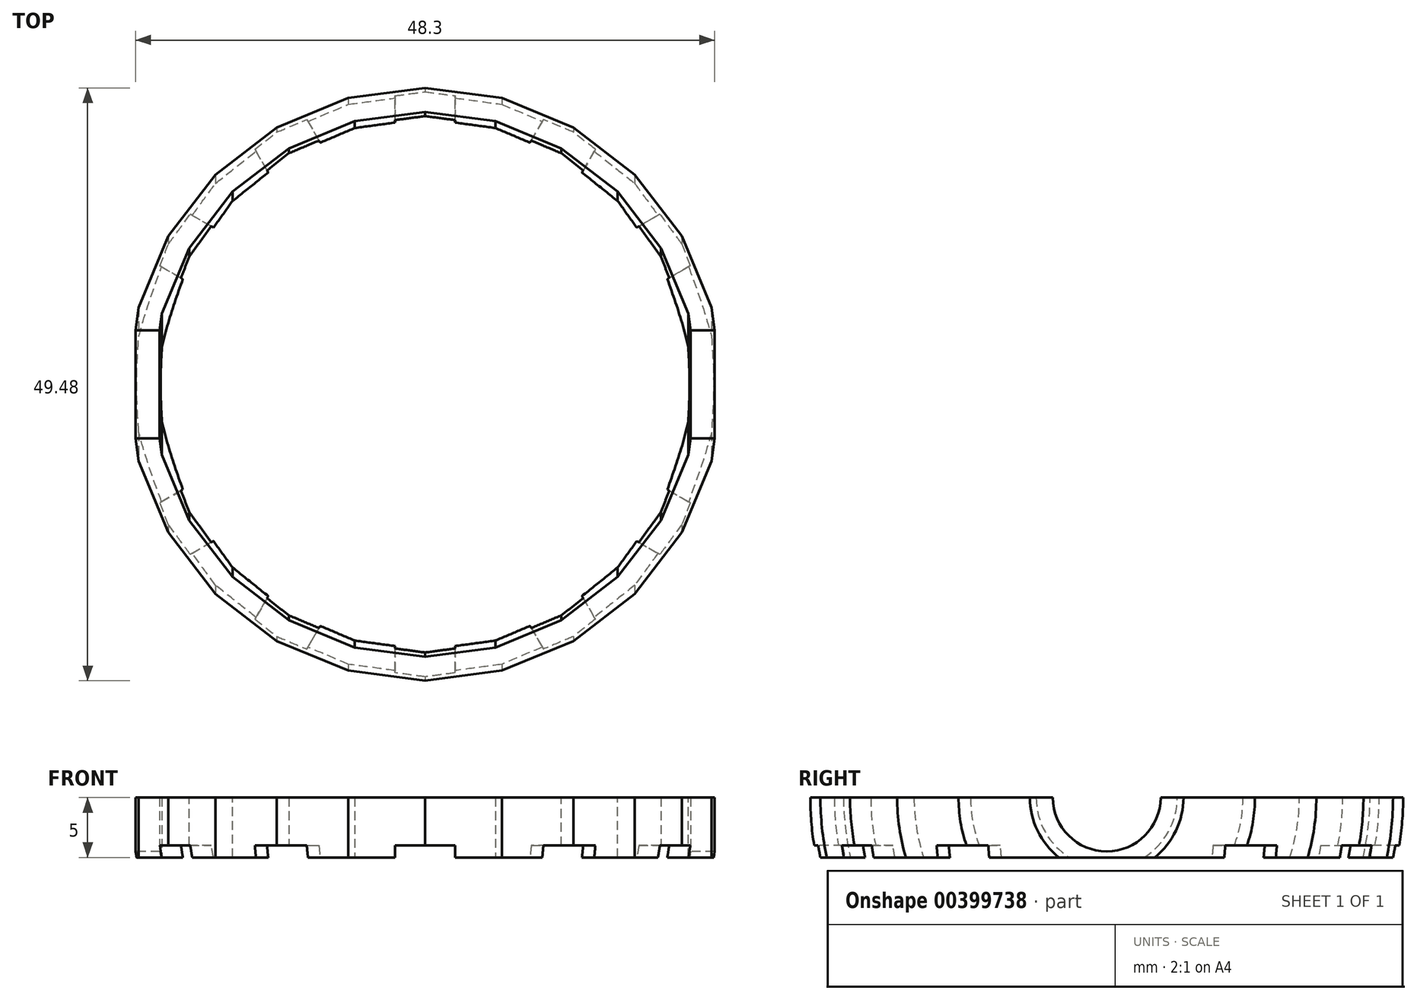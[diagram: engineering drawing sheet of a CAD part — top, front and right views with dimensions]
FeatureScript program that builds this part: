
annotation { "Feature Type Name" : "Feature", "Feature Type Description" : "" }
export const myFeature = defineFeature(function(context is Context, id is Id, definition is map)
    precondition{}
    {
        {
            var Q0;
            Q0=qCreatedBy(makeId("Top.planeOp"),FACE);
            var sketch = newSketch(context, id + "F0", { "sketchPlane" : qUnion([Q0])});
            skLineSegment(sketch, "E0", {"start": v(-24.74, 0) * mm, "end": v(24.74, 0) * mm});
            skLineSegment(sketch, "E1", {"start": v(-24.74, 0) * mm, "end": v(-22.74, 0) * mm});
            skLineSegment(sketch, "E2", {"start": v(24.74, 0) * mm, "end": v(22.74, 0) * mm});
            skLineSegment(sketch, "E3", {"start": v(0, 0) * mm, "end": v(-21.43, -12.37) * mm});
            skLineSegment(sketch, "E4", {"start": v(0, 0) * mm, "end": v(-23.9, -6.4) * mm});
            skLineSegment(sketch, "E5", {"start": v(-23.9, -6.4) * mm, "end": v(0, 0) * mm});
            skLineSegment(sketch, "E6", {"start": v(0, 0) * mm, "end": v(-17.5, -17.5) * mm});
            skLineSegment(sketch, "E7", {"start": v(-17.5, -17.5) * mm, "end": v(0, 0) * mm});
            skLineSegment(sketch, "E8", {"start": v(0, 0) * mm, "end": v(12.37, -21.43) * mm});
            skLineSegment(sketch, "E9", {"start": v(12.37, -21.43) * mm, "end": v(0, 0) * mm});
            skLineSegment(sketch, "E10", {"start": v(0, 0) * mm, "end": v(17.5, -17.5) * mm});
            skLineSegment(sketch, "E11", {"start": v(17.5, -17.5) * mm, "end": v(0, 0) * mm});
            skLineSegment(sketch, "E12", {"start": v(0, 0) * mm, "end": v(21.43, -12.37) * mm});
            skLineSegment(sketch, "E13", {"start": v(0, 0) * mm, "end": v(-12.37, -21.43) * mm});
            skLineSegment(sketch, "E14", {"start": v(-12.37, -21.43) * mm, "end": v(0, 0) * mm});
            skLineSegment(sketch, "E15", {"start": v(0, 0) * mm, "end": v(-6.4, -23.9) * mm});
            skLineSegment(sketch, "E16", {"start": v(0, 0) * mm, "end": v(6.4, -23.9) * mm});
            skLineSegment(sketch, "E17", {"start": v(0, 0) * mm, "end": v(23.9, -6.4) * mm});
            skLineSegment(sketch, "E18", {"start": v(0, 0) * mm, "end": v(0, -24.74) * mm});
            skSolve(sketch);
        }
        {
            var Q0;
            Q0=qCreatedBy(makeId("Top.planeOp"),FACE);
            var sketch = newSketch(context, id + "F1", { "sketchPlane" : qUnion([Q0])});
            skLineSegment(sketch, "E19", {"start": v(-24.74, 0) * mm, "end": v(-23.9, -6.4) * mm});
            skLineSegment(sketch, "E20", {"start": v(-23.9, -6.4) * mm, "end": v(-21.43, -12.37) * mm});
            skLineSegment(sketch, "E21", {"start": v(-21.43, -12.37) * mm, "end": v(-17.5, -17.5) * mm});
            skLineSegment(sketch, "E22", {"start": v(-17.5, -17.5) * mm, "end": v(-12.37, -21.43) * mm});
            skLineSegment(sketch, "E23", {"start": v(-12.37, -21.43) * mm, "end": v(-6.4, -23.9) * mm});
            skLineSegment(sketch, "E24", {"start": v(-6.4, -23.9) * mm, "end": v(0, -24.74) * mm});
            skLineSegment(sketch, "E25", {"start": v(0, -24.74) * mm, "end": v(6.4, -23.9) * mm});
            skLineSegment(sketch, "E26", {"start": v(6.4, -23.9) * mm, "end": v(12.37, -21.43) * mm});
            skLineSegment(sketch, "E27", {"start": v(12.37, -21.43) * mm, "end": v(17.5, -17.5) * mm});
            skLineSegment(sketch, "E28", {"start": v(17.5, -17.5) * mm, "end": v(21.43, -12.37) * mm});
            skLineSegment(sketch, "E29", {"start": v(21.43, -12.37) * mm, "end": v(23.9, -6.4) * mm});
            skLineSegment(sketch, "E30", {"start": v(23.9, -6.4) * mm, "end": v(24.74, 0) * mm});
            skLineSegment(sketch, "E31", {"start": v(-22.74, 0) * mm, "end": v(-21.97, -5.89) * mm});
            skLineSegment(sketch, "E32", {"start": v(-21.97, -5.89) * mm, "end": v(-19.7, -11.37) * mm});
            skLineSegment(sketch, "E33", {"start": v(-19.7, -11.37) * mm, "end": v(-16.08, -16.08) * mm});
            skLineSegment(sketch, "E34", {"start": v(-16.08, -16.08) * mm, "end": v(-11.37, -19.7) * mm});
            skLineSegment(sketch, "E35", {"start": v(-11.37, -19.7) * mm, "end": v(-5.89, -21.97) * mm});
            skLineSegment(sketch, "E36", {"start": v(-5.89, -21.97) * mm, "end": v(0, -22.74) * mm});
            skLineSegment(sketch, "E37", {"start": v(0, -22.74) * mm, "end": v(5.89, -21.97) * mm});
            skLineSegment(sketch, "E38", {"start": v(5.89, -21.97) * mm, "end": v(11.37, -19.7) * mm});
            skLineSegment(sketch, "E39", {"start": v(11.37, -19.7) * mm, "end": v(16.08, -16.08) * mm});
            skLineSegment(sketch, "E40", {"start": v(16.08, -16.08) * mm, "end": v(19.7, -11.37) * mm});
            skLineSegment(sketch, "E41", {"start": v(19.7, -11.37) * mm, "end": v(21.97, -5.89) * mm});
            skLineSegment(sketch, "E42", {"start": v(21.97, -5.89) * mm, "end": v(22.74, 0) * mm});
            skLineSegment(sketch, "E43", {"start": v(-24.74, 0) * mm, "end": v(-22.74, 0) * mm});
            skLineSegment(sketch, "E44", {"start": v(22.74, 0) * mm, "end": v(24.74, 0) * mm});
            skSolve(sketch);
        }
        {
            var Q0;
            Q0=qSketchRegion(id+"F1",true);
            var Q1;
            Q1=sQuery(id+"F0.wireOp",EDGE,"E0");
            revolve(context, id + "F2", {"entities" : qUnion([Q0]), "axis" : qUnion([Q1]), "revolveType" : RevolveType.FULL});
        }
        {
            var Q0;
            Q0=qCreatedBy(makeId("Top.planeOp"),FACE);
            var sketch = newSketch(context, id + "F3", { "sketchPlane" : qUnion([Q0])});
            skLineSegment(sketch, "E45.bottom", {"start": v(-24.99, 25) * mm, "end": v(24.99, 25) * mm});
            skLineSegment(sketch, "E45.top", {"start": v(-24.99, -25) * mm, "end": v(24.99, -25) * mm});
            skLineSegment(sketch, "E45.left", {"start": v(-24.99, 25) * mm, "end": v(-24.99, -25) * mm});
            skLineSegment(sketch, "E45.right", {"start": v(24.99, 25) * mm, "end": v(24.99, -25) * mm});
            skPoint(sketch, "E45.middle", {"position": v(0, 0) * mm});
            skSolve(sketch);
        }
        {
            var Q0;
            Q0=qSketchRegion(id+"F3",true);
            extrude(context, id + "F4", {"entities" : qUnion([Q0]), "operationType" : NewBodyOperationType.REMOVE, "depth" : 25 * mm});
        }
        {
            var Q0;
            Q0=qCreatedBy(makeId("Top.planeOp"),FACE);
            var sketch = newSketch(context, id + "F5", { "sketchPlane" : qUnion([Q0])});
            skLineSegment(sketch, "E46", {"start": v(-22.74, 0) * mm, "end": v(-21.97, -5.89) * mm});
            skLineSegment(sketch, "E47", {"start": v(-21.97, -5.89) * mm, "end": v(-19.7, -11.37) * mm});
            skLineSegment(sketch, "E48", {"start": v(-19.7, -11.37) * mm, "end": v(-16.08, -16.08) * mm});
            skLineSegment(sketch, "E49", {"start": v(-16.08, -16.08) * mm, "end": v(-11.37, -19.7) * mm});
            skLineSegment(sketch, "E50", {"start": v(-11.37, -19.7) * mm, "end": v(-5.89, -21.97) * mm});
            skLineSegment(sketch, "E51", {"start": v(-5.89, -21.97) * mm, "end": v(0, -22.74) * mm});
            skLineSegment(sketch, "E52", {"start": v(0, -22.74) * mm, "end": v(5.89, -21.97) * mm});
            skLineSegment(sketch, "E53", {"start": v(5.89, -21.97) * mm, "end": v(11.37, -19.7) * mm});
            skLineSegment(sketch, "E54", {"start": v(11.37, -19.7) * mm, "end": v(16.08, -16.08) * mm});
            skLineSegment(sketch, "E55", {"start": v(16.08, -16.08) * mm, "end": v(19.7, -11.37) * mm});
            skLineSegment(sketch, "E56", {"start": v(19.7, -11.37) * mm, "end": v(21.97, -5.89) * mm});
            skLineSegment(sketch, "E57", {"start": v(21.97, -5.89) * mm, "end": v(22.74, 0) * mm});
            skLineSegment(sketch, "E58", {"start": v(20.74, 0) * mm, "end": v(20.03, -5.37) * mm});
            skLineSegment(sketch, "E59", {"start": v(20.03, -5.37) * mm, "end": v(17.96, -10.37) * mm});
            skLineSegment(sketch, "E60", {"start": v(17.96, -10.37) * mm, "end": v(14.67, -14.67) * mm});
            skLineSegment(sketch, "E61", {"start": v(14.67, -14.67) * mm, "end": v(10.37, -17.96) * mm});
            skLineSegment(sketch, "E62", {"start": v(10.37, -17.96) * mm, "end": v(5.37, -20.03) * mm});
            skLineSegment(sketch, "E63", {"start": v(5.37, -20.03) * mm, "end": v(0, -20.74) * mm});
            skLineSegment(sketch, "E64", {"start": v(0, -20.74) * mm, "end": v(-5.37, -20.03) * mm});
            skLineSegment(sketch, "E65", {"start": v(-5.37, -20.03) * mm, "end": v(-10.37, -17.96) * mm});
            skLineSegment(sketch, "E66", {"start": v(-10.37, -17.96) * mm, "end": v(-14.67, -14.67) * mm});
            skLineSegment(sketch, "E67", {"start": v(-14.67, -14.67) * mm, "end": v(-17.96, -10.37) * mm});
            skLineSegment(sketch, "E68", {"start": v(-17.96, -10.37) * mm, "end": v(-20.03, -5.37) * mm});
            skLineSegment(sketch, "E69", {"start": v(-20.03, -5.37) * mm, "end": v(-20.74, 0) * mm});
            skLineSegment(sketch, "E70", {"start": v(-20.74, 0) * mm, "end": v(-22.74, 0) * mm});
            skLineSegment(sketch, "E71", {"start": v(20.74, 0) * mm, "end": v(22.74, 0) * mm});
            skSolve(sketch);
        }
        {
            var Q0;
            Q0=qSketchRegion(id+"F5",true);
            var Q1;
            Q1=sQuery(id+"F0.wireOp",EDGE,"E0");
            revolve(context, id + "F6", {"entities" : qUnion([Q0]), "axis" : qUnion([Q1]), "revolveType" : RevolveType.FULL, "oppositeDirection" : true});
        }
        {
            var Q0;
            Q0=qCreatedBy(makeId("Top.planeOp"),FACE);
            var sketch = newSketch(context, id + "F7", { "sketchPlane" : qUnion([Q0])});
            skLineSegment(sketch, "E72.bottom", {"start": v(-27.5, 27.5) * mm, "end": v(27.5, 27.5) * mm});
            skLineSegment(sketch, "E72.top", {"start": v(-27.5, -27.5) * mm, "end": v(27.5, -27.5) * mm});
            skLineSegment(sketch, "E72.left", {"start": v(-27.5, 27.5) * mm, "end": v(-27.5, -27.5) * mm});
            skLineSegment(sketch, "E72.right", {"start": v(27.5, 27.5) * mm, "end": v(27.5, -27.5) * mm});
            skPoint(sketch, "E72.middle", {"position": v(0, 0) * mm});
            skSolve(sketch);
        }
        {
            var Q0;
            Q0=qSketchRegion(id+"F7",true);
            extrude(context, id + "F8", {"entities" : qUnion([Q0]), "operationType" : NewBodyOperationType.REMOVE, "depth" : 25 * mm, "hasSecondDirection" : true, "secondDirectionOppositeDirection" : false, "secondDirectionDepth" : 5 * mm});
        }
        {
            var Q0;
            Q0=qCreatedBy(makeId("Top.planeOp"),FACE);
            var sketch = newSketch(context, id + "F9", { "sketchPlane" : qUnion([Q0])});
            skLineSegment(sketch, "E73.bottom", {"start": v(-30, 30) * mm, "end": v(30, 30) * mm});
            skLineSegment(sketch, "E73.top", {"start": v(-30, -30) * mm, "end": v(30, -30) * mm});
            skLineSegment(sketch, "E73.left", {"start": v(-30, 30) * mm, "end": v(-30, -30) * mm});
            skLineSegment(sketch, "E73.right", {"start": v(30, 30) * mm, "end": v(30, -30) * mm});
            skPoint(sketch, "E73.middle", {"position": v(0, 0) * mm});
            skSolve(sketch);
        }
        {
            var Q0;
            Q0=qSketchRegion(id+"F9",true);
            extrude(context, id + "F10", {"entities" : qUnion([Q0]), "operationType" : NewBodyOperationType.REMOVE, "oppositeDirection" : true, "depth" : 25 * mm, "hasSecondDirection" : true, "secondDirectionOppositeDirection" : true, "secondDirectionDepth" : 5 * mm});
        }
        {
            var Q0;
            Q0=qCreatedBy(makeId("Right.planeOp"),FACE);
            var sketch = newSketch(context, id + "F11", { "sketchPlane" : qUnion([Q0])});
            skCircle(sketch, "E74", {"center": v(0, 0) * mm, "radius": 4.5 * mm});
            skSolve(sketch);
        }
        {
            var Q0;
            Q0=qSketchRegion(id+"F11",true);
            extrude(context, id + "F12", {"entities" : qUnion([Q0]), "operationType" : NewBodyOperationType.REMOVE, "depth" : 25 * mm, "hasSecondDirection" : true, "secondDirectionOppositeDirection" : true, "secondDirectionDepth" : 25 * mm});
        }
        {
            var Q0;
            Q0=makeQuery(id+"F8.boolean.opBoolean","INTERSECT",EDGE,{"disambiguationData":[OD(0.0)],"derivedFrom":[makeQuery(id+"F6.opRevolve","SWEPT_FACE",FACE,{"disambiguationData":[OSD([sQuery(id+"F5.wireOp",EDGE,"E48")])]}),makeQuery(id+"F8.opExtrude","CAP_FACE",FACE,{"disambiguationData":[OSD([sQuery(id+"F7.wireOp",EDGE,"E72.bottom"),sQuery(id+"F7.wireOp",EDGE,"E72.top"),sQuery(id+"F7.wireOp",EDGE,"E72.left"),sQuery(id+"F7.wireOp",EDGE,"E72.right")])],"isStart":true})]});
            var Q1;
            Q1=makeQuery(id+"F8.boolean.opBoolean","INTERSECT",EDGE,{"disambiguationData":[OD(0.0)],"derivedFrom":[makeQuery(id+"F6.opRevolve","SWEPT_FACE",FACE,{"disambiguationData":[OSD([sQuery(id+"F5.wireOp",EDGE,"E50")])]}),makeQuery(id+"F8.opExtrude","CAP_FACE",FACE,{"disambiguationData":[OSD([sQuery(id+"F7.wireOp",EDGE,"E72.bottom"),sQuery(id+"F7.wireOp",EDGE,"E72.top"),sQuery(id+"F7.wireOp",EDGE,"E72.left"),sQuery(id+"F7.wireOp",EDGE,"E72.right")])],"isStart":true})]});
            var Q2;
            Q2=makeQuery(id+"F8.boolean.opBoolean","INTERSECT",EDGE,{"disambiguationData":[OD(0.0)],"derivedFrom":[makeQuery(id+"F6.opRevolve","SWEPT_FACE",FACE,{"disambiguationData":[OSD([sQuery(id+"F5.wireOp",EDGE,"E52")])]}),makeQuery(id+"F8.opExtrude","CAP_FACE",FACE,{"disambiguationData":[OSD([sQuery(id+"F7.wireOp",EDGE,"E72.bottom"),sQuery(id+"F7.wireOp",EDGE,"E72.top"),sQuery(id+"F7.wireOp",EDGE,"E72.left"),sQuery(id+"F7.wireOp",EDGE,"E72.right")])],"isStart":true})]});
            var Q3;
            Q3=makeQuery(id+"F8.boolean.opBoolean","INTERSECT",EDGE,{"disambiguationData":[OD(0.0)],"derivedFrom":[makeQuery(id+"F6.opRevolve","SWEPT_FACE",FACE,{"disambiguationData":[OSD([sQuery(id+"F5.wireOp",EDGE,"E54")])]}),makeQuery(id+"F8.opExtrude","CAP_FACE",FACE,{"disambiguationData":[OSD([sQuery(id+"F7.wireOp",EDGE,"E72.bottom"),sQuery(id+"F7.wireOp",EDGE,"E72.top"),sQuery(id+"F7.wireOp",EDGE,"E72.left"),sQuery(id+"F7.wireOp",EDGE,"E72.right")])],"isStart":true})]});
            var Q4;
            Q4=makeQuery(id+"F8.boolean.opBoolean","INTERSECT",EDGE,{"disambiguationData":[OD(1.0)],"derivedFrom":[makeQuery(id+"F6.opRevolve","SWEPT_FACE",FACE,{"disambiguationData":[OSD([sQuery(id+"F5.wireOp",EDGE,"E55")])]}),makeQuery(id+"F8.opExtrude","CAP_FACE",FACE,{"disambiguationData":[OSD([sQuery(id+"F7.wireOp",EDGE,"E72.bottom"),sQuery(id+"F7.wireOp",EDGE,"E72.top"),sQuery(id+"F7.wireOp",EDGE,"E72.left"),sQuery(id+"F7.wireOp",EDGE,"E72.right")])],"isStart":true})]});
            var Q5;
            Q5=makeQuery(id+"F8.boolean.opBoolean","INTERSECT",EDGE,{"disambiguationData":[OD(1.0)],"derivedFrom":[makeQuery(id+"F6.opRevolve","SWEPT_FACE",FACE,{"disambiguationData":[OSD([sQuery(id+"F5.wireOp",EDGE,"E53")])]}),makeQuery(id+"F8.opExtrude","CAP_FACE",FACE,{"disambiguationData":[OSD([sQuery(id+"F7.wireOp",EDGE,"E72.bottom"),sQuery(id+"F7.wireOp",EDGE,"E72.top"),sQuery(id+"F7.wireOp",EDGE,"E72.left"),sQuery(id+"F7.wireOp",EDGE,"E72.right")])],"isStart":true})]});
            var Q6;
            Q6=makeQuery(id+"F8.boolean.opBoolean","INTERSECT",EDGE,{"disambiguationData":[OD(1.0)],"derivedFrom":[makeQuery(id+"F6.opRevolve","SWEPT_FACE",FACE,{"disambiguationData":[OSD([sQuery(id+"F5.wireOp",EDGE,"E51")])]}),makeQuery(id+"F8.opExtrude","CAP_FACE",FACE,{"disambiguationData":[OSD([sQuery(id+"F7.wireOp",EDGE,"E72.bottom"),sQuery(id+"F7.wireOp",EDGE,"E72.top"),sQuery(id+"F7.wireOp",EDGE,"E72.left"),sQuery(id+"F7.wireOp",EDGE,"E72.right")])],"isStart":true})]});
            var Q7;
            Q7=makeQuery(id+"F8.boolean.opBoolean","INTERSECT",EDGE,{"disambiguationData":[OD(1.0)],"derivedFrom":[makeQuery(id+"F6.opRevolve","SWEPT_FACE",FACE,{"disambiguationData":[OSD([sQuery(id+"F5.wireOp",EDGE,"E49")])]}),makeQuery(id+"F8.opExtrude","CAP_FACE",FACE,{"disambiguationData":[OSD([sQuery(id+"F7.wireOp",EDGE,"E72.bottom"),sQuery(id+"F7.wireOp",EDGE,"E72.top"),sQuery(id+"F7.wireOp",EDGE,"E72.left"),sQuery(id+"F7.wireOp",EDGE,"E72.right")])],"isStart":true})]});
            var Q8;
            Q8=makeQuery(id+"F8.boolean.opBoolean","INTERSECT",EDGE,{"disambiguationData":[OD(0.0)],"derivedFrom":[makeQuery(id+"F6.opRevolve","SWEPT_FACE",FACE,{"disambiguationData":[OSD([sQuery(id+"F5.wireOp",EDGE,"E56")])]}),makeQuery(id+"F8.opExtrude","CAP_FACE",FACE,{"disambiguationData":[OSD([sQuery(id+"F7.wireOp",EDGE,"E72.bottom"),sQuery(id+"F7.wireOp",EDGE,"E72.top"),sQuery(id+"F7.wireOp",EDGE,"E72.left"),sQuery(id+"F7.wireOp",EDGE,"E72.right")])],"isStart":true})]});
            var Q9;
            Q9=makeQuery(id+"F8.boolean.opBoolean","INTERSECT",EDGE,{"disambiguationData":[OD(1.0)],"derivedFrom":[makeQuery(id+"F6.opRevolve","SWEPT_FACE",FACE,{"disambiguationData":[OSD([sQuery(id+"F5.wireOp",EDGE,"E47")])]}),makeQuery(id+"F8.opExtrude","CAP_FACE",FACE,{"disambiguationData":[OSD([sQuery(id+"F7.wireOp",EDGE,"E72.bottom"),sQuery(id+"F7.wireOp",EDGE,"E72.top"),sQuery(id+"F7.wireOp",EDGE,"E72.left"),sQuery(id+"F7.wireOp",EDGE,"E72.right")])],"isStart":true})]});
            chamfer(context, id + "F13", {"entities" : qUnion([Q0, Q1, Q2, Q3, Q4, Q5, Q6, Q7, Q8, Q9]), "chamferType" : ChamferType.OFFSET_ANGLE, "width" : 0.5 * mm, "oppositeDirection" : false, "angle" : 60 * degree, "tangentPropagation" : true});
        }
        {
            var Q0;
            Q0=qCreatedBy(makeId("Right.planeOp"),FACE);
            var sketch = newSketch(context, id + "F14", { "sketchPlane" : qUnion([Q0])});
            skLineSegment(sketch, "E75", {"start": v(0, 0) * mm, "end": v(0, 50) * mm});
            skLineSegment(sketch, "E76", {"start": v(0, 0) * mm, "end": v(0, -50) * mm});
            skSolve(sketch);
        }
        {
            var Q0;
            Q0=sQuery(id+"F14.wireOp",VERTEX,"E75.end");
            var Q1;
            Q1=sQuery(id+"F14.wireOp",VERTEX,"E76.end");
            var Q2;
            Q2=sQuery(id+"F0.wireOp",VERTEX,"E3.end");
            cPlane(context, id + "F15", {"entities" : qUnion([Q0, Q1, Q2]), "cplaneType" : CPlaneType.THREE_POINT, "offset" : 25 * mm, "width" : 150 * mm, "height" : 150 * mm});
        }
        {
            var Q0;
            Q0=sQuery(id+"F0.wireOp",VERTEX,"E14.start");
            var Q1;
            Q1=sQuery(id+"F14.wireOp",VERTEX,"E76.end");
            var Q2;
            Q2=sQuery(id+"F14.wireOp",VERTEX,"E75.end");
            cPlane(context, id + "F16", {"entities" : qUnion([Q0, Q1, Q2]), "cplaneType" : CPlaneType.THREE_POINT, "offset" : 25 * mm, "width" : 150 * mm, "height" : 150 * mm});
        }
        {
            var Q0;
            Q0=sQuery(id+"F0.wireOp",VERTEX,"E8.end");
            var Q1;
            Q1=sQuery(id+"F14.wireOp",VERTEX,"E76.end");
            var Q2;
            Q2=sQuery(id+"F14.wireOp",VERTEX,"E75.end");
            cPlane(context, id + "F17", {"entities" : qUnion([Q0, Q1, Q2]), "cplaneType" : CPlaneType.THREE_POINT, "offset" : 25 * mm, "width" : 150 * mm, "height" : 150 * mm});
        }
        {
            var Q0;
            Q0=sQuery(id+"F0.wireOp",VERTEX,"E12.end");
            var Q1;
            Q1=sQuery(id+"F14.wireOp",VERTEX,"E76.end");
            var Q2;
            Q2=sQuery(id+"F14.wireOp",VERTEX,"E75.end");
            cPlane(context, id + "F18", {"entities" : qUnion([Q0, Q1, Q2]), "cplaneType" : CPlaneType.THREE_POINT, "offset" : 25 * mm, "width" : 150 * mm, "height" : 150 * mm});
        }
        {
            var Q0;
            Q0=sQuery(id+"F0.wireOp",VERTEX,"E17.end");
            var Q1;
            Q1=sQuery(id+"F14.wireOp",VERTEX,"E76.end");
            var Q2;
            Q2=sQuery(id+"F14.wireOp",VERTEX,"E75.end");
            cPlane(context, id + "F19", {"entities" : qUnion([Q0, Q1, Q2]), "cplaneType" : CPlaneType.THREE_POINT, "offset" : 25 * mm, "width" : 150 * mm, "height" : 150 * mm});
        }
        {
            var Q0;
            Q0=qCreatedBy(makeId("Front.planeOp"),FACE);
            var sketch = newSketch(context, id + "F20", { "sketchPlane" : qUnion([Q0])});
            skLineSegment(sketch, "E77.bottom", {"start": v(2.5, -19) * mm, "end": v(-2.5, -19) * mm});
            skLineSegment(sketch, "E77.top", {"start": v(2.5, -4) * mm, "end": v(-2.5, -4) * mm});
            skLineSegment(sketch, "E77.left", {"start": v(2.5, -19) * mm, "end": v(2.5, -4) * mm});
            skLineSegment(sketch, "E77.right", {"start": v(-2.5, -19) * mm, "end": v(-2.5, -4) * mm});
            skPoint(sketch, "E77.middle", {"position": v(0, -11.5) * mm});
            skSolve(sketch);
        }
        {
            var Q0;
            Q0=qSketchRegion(id+"F20",true);
            extrude(context, id + "F21", {"entities" : qUnion([Q0]), "operationType" : NewBodyOperationType.REMOVE, "oppositeDirection" : true, "depth" : 25 * mm, "hasSecondDirection" : true, "secondDirectionOppositeDirection" : false, "secondDirectionDepth" : 25 * mm});
        }
        {
            var Q0;
            Q0=qCreatedBy(id+"F18.planeOp",FACE);
            var sketch = newSketch(context, id + "F22", { "sketchPlane" : qUnion([Q0])});
            skLineSegment(sketch, "E78.bottom", {"start": v(2.5, -19) * mm, "end": v(-2.5, -19) * mm});
            skLineSegment(sketch, "E78.top", {"start": v(2.5, -4) * mm, "end": v(-2.5, -4) * mm});
            skLineSegment(sketch, "E78.left", {"start": v(2.5, -19) * mm, "end": v(2.5, -4) * mm});
            skLineSegment(sketch, "E78.right", {"start": v(-2.5, -19) * mm, "end": v(-2.5, -4) * mm});
            skPoint(sketch, "E78.middle", {"position": v(0, -11.5) * mm});
            skSolve(sketch);
        }
        {
            var Q0;
            Q0=qSketchRegion(id+"F22",true);
            extrude(context, id + "F23", {"entities" : qUnion([Q0]), "operationType" : NewBodyOperationType.REMOVE, "depth" : 25 * mm, "hasSecondDirection" : true, "secondDirectionOppositeDirection" : true, "secondDirectionDepth" : 25 * mm});
        }
        {
            var Q0;
            Q0=qCreatedBy(id+"F17.planeOp",FACE);
            var sketch = newSketch(context, id + "F24", { "sketchPlane" : qUnion([Q0])});
            skLineSegment(sketch, "E79.bottom", {"start": v(2.5, -19) * mm, "end": v(-2.5, -19) * mm});
            skLineSegment(sketch, "E79.top", {"start": v(2.5, -4) * mm, "end": v(-2.5, -4) * mm});
            skLineSegment(sketch, "E79.left", {"start": v(2.5, -19) * mm, "end": v(2.5, -4) * mm});
            skLineSegment(sketch, "E79.right", {"start": v(-2.5, -19) * mm, "end": v(-2.5, -4) * mm});
            skPoint(sketch, "E79.middle", {"position": v(0, -11.5) * mm});
            skSolve(sketch);
        }
        {
            var Q0;
            Q0=qSketchRegion(id+"F24",true);
            extrude(context, id + "F25", {"entities" : qUnion([Q0]), "operationType" : NewBodyOperationType.REMOVE, "oppositeDirection" : true, "depth" : 25 * mm, "hasSecondDirection" : true, "secondDirectionOppositeDirection" : false, "secondDirectionDepth" : 25 * mm});
        }
        {
            var Q0;
            Q0=qCreatedBy(id+"F15.planeOp",FACE);
            var sketch = newSketch(context, id + "F26", { "sketchPlane" : qUnion([Q0])});
            skLineSegment(sketch, "E80.bottom", {"start": v(2.5, -4) * mm, "end": v(-2.5, -4) * mm});
            skLineSegment(sketch, "E80.top", {"start": v(2.5, -19) * mm, "end": v(-2.5, -19) * mm});
            skLineSegment(sketch, "E80.left", {"start": v(2.5, -4) * mm, "end": v(2.5, -19) * mm});
            skLineSegment(sketch, "E80.right", {"start": v(-2.5, -4) * mm, "end": v(-2.5, -19) * mm});
            skPoint(sketch, "E80.middle", {"position": v(0, -11.5) * mm});
            skSolve(sketch);
        }
        {
            var Q0;
            Q0=qSketchRegion(id+"F26",true);
            extrude(context, id + "F27", {"entities" : qUnion([Q0]), "operationType" : NewBodyOperationType.REMOVE, "oppositeDirection" : true, "depth" : 25 * mm, "hasSecondDirection" : true, "secondDirectionOppositeDirection" : false, "secondDirectionDepth" : 25 * mm});
        }
        {
            var Q0;
            Q0=qCreatedBy(id+"F16.planeOp",FACE);
            var sketch = newSketch(context, id + "F28", { "sketchPlane" : qUnion([Q0])});
            skLineSegment(sketch, "E81.bottom", {"start": v(-2.5, -4) * mm, "end": v(2.5, -4) * mm});
            skLineSegment(sketch, "E81.top", {"start": v(-2.5, -19) * mm, "end": v(2.5, -19) * mm});
            skLineSegment(sketch, "E81.left", {"start": v(-2.5, -4) * mm, "end": v(-2.5, -19) * mm});
            skLineSegment(sketch, "E81.right", {"start": v(2.5, -4) * mm, "end": v(2.5, -19) * mm});
            skPoint(sketch, "E81.middle", {"position": v(0, -11.5) * mm});
            skSolve(sketch);
        }
        {
            var Q0;
            Q0=qSketchRegion(id+"F28",true);
            extrude(context, id + "F29", {"entities" : qUnion([Q0]), "operationType" : NewBodyOperationType.REMOVE, "depth" : 25 * mm, "hasSecondDirection" : true, "secondDirectionOppositeDirection" : true, "secondDirectionDepth" : 25 * mm});
        }
        {
            var Q0;
            Q0=qCreatedBy(makeId("Right.planeOp"),FACE);
            var sketch = newSketch(context, id + "F30", { "sketchPlane" : qUnion([Q0])});
            skLineSegment(sketch, "E82.bottom", {"start": v(2.5, -19) * mm, "end": v(-2.5, -19) * mm});
            skLineSegment(sketch, "E82.top", {"start": v(2.5, -9) * mm, "end": v(-2.5, -9) * mm});
            skLineSegment(sketch, "E82.left", {"start": v(2.5, -19) * mm, "end": v(2.5, -9) * mm});
            skLineSegment(sketch, "E82.right", {"start": v(-2.5, -19) * mm, "end": v(-2.5, -9) * mm});
            skPoint(sketch, "E82.middle", {"position": v(0, -14) * mm});
            skSolve(sketch);
        }
        {
            var Q0;
            Q0=qSketchRegion(id+"F30",true);
            extrude(context, id + "F31", {"entities" : qUnion([Q0]), "operationType" : NewBodyOperationType.REMOVE, "oppositeDirection" : true, "depth" : 25 * mm, "hasSecondDirection" : true, "secondDirectionOppositeDirection" : false, "secondDirectionDepth" : 25 * mm});
        }
        {
            var Q0;
            Q0=qCreatedBy(makeId("Top.planeOp"),FACE);
            var sketch = newSketch(context, id + "F32", { "sketchPlane" : qUnion([Q0])});
            skCircle(sketch, "E83.cCircle", {"center": v(0, 0) * mm, "radius": 5.72 * mm, "construction": true});
            skLineSegment(sketch, "E83.0", {"start": v(-4.95, 2.85) * mm, "end": v(0, 5.72) * mm});
            skLineSegment(sketch, "E83.1", {"start": v(0, 5.72) * mm, "end": v(4.94, 2.87) * mm});
            skLineSegment(sketch, "E83.2", {"start": v(4.94, 2.87) * mm, "end": v(4.95, -2.85) * mm});
            skLineSegment(sketch, "E83.3", {"start": v(4.95, -2.85) * mm, "end": v(0, -5.72) * mm});
            skLineSegment(sketch, "E83.4", {"start": v(0, -5.72) * mm, "end": v(-4.94, -2.87) * mm});
            skLineSegment(sketch, "E83.5", {"start": v(-4.94, -2.87) * mm, "end": v(-4.95, 2.85) * mm});
            skSolve(sketch);
        }
        {
            var Q0;
            Q0=qSketchRegion(id+"F32",true);
            extrude(context, id + "F33", {"entities" : qUnion([Q0]), "operationType" : NewBodyOperationType.REMOVE, "oppositeDirection" : true, "depth" : 25 * mm, "hasSecondDirection" : true, "secondDirectionOppositeDirection" : false, "secondDirectionDepth" : 25 * mm});
        }
        {
            var Q0;
            Q0=makeQuery(id+"F6.opRevolve","SWEPT_BODY",BODY,{"disambiguationData":[OSD([sQuery(id+"F5.wireOp",EDGE,"E46"),sQuery(id+"F5.wireOp",EDGE,"E47"),sQuery(id+"F5.wireOp",EDGE,"E48"),sQuery(id+"F5.wireOp",EDGE,"E49"),sQuery(id+"F5.wireOp",EDGE,"E50"),sQuery(id+"F5.wireOp",EDGE,"E51"),sQuery(id+"F5.wireOp",EDGE,"E52"),sQuery(id+"F5.wireOp",EDGE,"E53"),sQuery(id+"F5.wireOp",EDGE,"E54"),sQuery(id+"F5.wireOp",EDGE,"E55"),sQuery(id+"F5.wireOp",EDGE,"E56"),sQuery(id+"F5.wireOp",EDGE,"E57"),sQuery(id+"F5.wireOp",EDGE,"E58"),sQuery(id+"F5.wireOp",EDGE,"E59"),sQuery(id+"F5.wireOp",EDGE,"E60"),sQuery(id+"F5.wireOp",EDGE,"E61"),sQuery(id+"F5.wireOp",EDGE,"E62"),sQuery(id+"F5.wireOp",EDGE,"E63"),sQuery(id+"F5.wireOp",EDGE,"E64"),sQuery(id+"F5.wireOp",EDGE,"E65"),sQuery(id+"F5.wireOp",EDGE,"E66"),sQuery(id+"F5.wireOp",EDGE,"E67"),sQuery(id+"F5.wireOp",EDGE,"E68"),sQuery(id+"F5.wireOp",EDGE,"E69"),sQuery(id+"F5.wireOp",EDGE,"E70"),sQuery(id+"F5.wireOp",EDGE,"E71")])]});
            deleteBodies(context, id + "F34", {"entities" : qUnion([Q0])});
        }
    });
